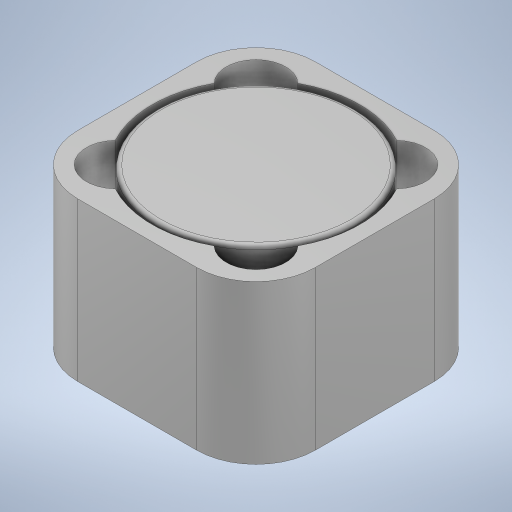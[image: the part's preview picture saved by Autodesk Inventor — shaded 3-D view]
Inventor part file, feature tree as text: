
AUTODESK INVENTOR PART (.ipt)
format: ipt  version: 2024.1 (Build 281209000, 209)  size: 253,440 bytes
history: native  units: mm
features: extrude x2, fillet x2, sketch x2, other x1
ambient origin geometry x8: Origin, YZ Plane, XZ Plane, XY Plane, X Axis, Y Axis, Z Axis, Center Point
bodies: Body1 (feature_tree)
feature tree (7):
  other  "ソリッド1"
  extrude  "押し出し1"  Depth=12.0mm
  fillet  "フィレット1"  Radius=8.0mm
  extrude  "押し出し2"  Depth=3.0mm
  fillet  "フィレット2"  Radius=10.0mm
  sketch  "スケッチ1"
  sketch  "スケッチ2"
